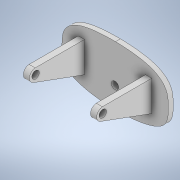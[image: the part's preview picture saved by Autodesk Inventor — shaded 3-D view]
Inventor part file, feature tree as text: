
AUTODESK INVENTOR PART (.ipt)
format: ipt  version: 2020.3 (Build 243373000, 373)  size: 154,624 bytes
history: native  units: in
note: dims shown in document units (in); Inventor stores cm internally (conversion verified against a paired STEP export)
features: extrude x3, sketch x3, projected_geometry x1
ambient origin geometry x8: Origin, YZ Plane, XZ Plane, XY Plane, X Axis, Y Axis, Z Axis, Center Point
bodies: Solid1 (feature_tree)
feature tree (7):
  extrude  "Extrusion1"  Depth=1.9685in TaperAngle=0.0deg
  extrude  "Extrusion2"  Depth=0.7874in
  extrude  "Extrusion3"  Depth=0.5343in TaperAngle=0.0deg
  sketch  "Sketch1"  dims[d0=0.1575in d1=0.0in d9=1.9685in d10=0.0in]
  sketch  "Sketch2"  dims[d11=1.5748in d12=0.7874in]
  sketch  "Sketch3"  dims[d13=0.2362in d14=0.5343in d15=0.0in]
  projected_geometry  "Projected Loop1"
